# Revit family: Urbane II Rail Shower w 300mm Overhead + Hand Shower
name_source: partatom
category: Specialty Equipment
units: mm (PartAtom-declared; Revit-internal decimal feet)

## family parameters
Cut with Voids When Loaded = No
Host = Face
OmniClass Number = 23.45.05.14.17
OmniClass Title = Showers
Part Type = Normal
Room Calculation Point = No
Round Connector Dimension = Use Radius
Shared = No

## types (5) — shared parameters
Assembly Code = D2010710
Default Elevation = 1000 mm  [stored 3.28084 ft]
Manufacturer = GWA Bathrooms & Kitchens
Material_Spray = GWA-Plastic-General
URL = https://www.caroma.com.au

## per-type parameters (varying)
| type | HandShower | Material_Base | Model | RainShower |
| Urbane II Rail Shower w/ 300mm Overhead  + Hand Shower - Chrome | Urbane II Hand Shower : Urbane II Hand Shower - Round - Chrome | GWA_Metal-Chrome | 99630C3 | Urbane II Rain Shower - 300mm Round : Urbane II Rain Shower - 300mm Round - Chrome |
| Urbane II Rail Shower w/ 300mm Overhead  + Hand Shower - Matte Black | Urbane II Hand Shower : Urbane II Hand Shower - Round - Matte Black | GWA-Metal-Black | 99630B3 | Urbane II Rain Shower - 300mm Round : Urbane II Rain Shower - 300mm Round - Matte Black |
| Urbane II Rail Shower w/ 300mm Overhead  + Hand Shower - Brushed Brass | Urbane II Hand Shower : Urbane II Hand Shower - Round - Brushed Brass | GWA_Metal-Brushed-Brass | 99630BB3 | Urbane II Rain Shower - 300mm Round : Urbane II Rain Shower - 300mm Round - Brushed Brass |
| Urbane II Rail Shower w/ 300mm Overhead  + Hand Shower - Gunmetal | Urbane II Hand Shower : Urbane II Hand Shower - Round - Gunmetal | GWA-Metal-Gunmetal Grey | 99630GM3 | Urbane II Rain Shower - 300mm Round : Urbane II Rain Shower - 300mm Round - Gunmetal |
| Urbane II Rail Shower w/ 300mm Overhead  + Hand Shower - Brushed Nickel | Urbane II Hand Shower : Urbane II Hand Shower - Round - Chrome | GWA_Metal-Brushed-Nickel | 99630BN3 | Urbane II Rain Shower - 300mm Round : Urbane II Rain Shower - 300mm Round - Chrome |

note: column(s) folded — value = type name in every type: Description

note: [stored X ft] marks values corroborated as IEEE doubles in the binary element streams (Revit-internal decimal feet)

## geometry (parser evidence)
native form markers: Sweep x7
no freeform markers — native parametric forms only
